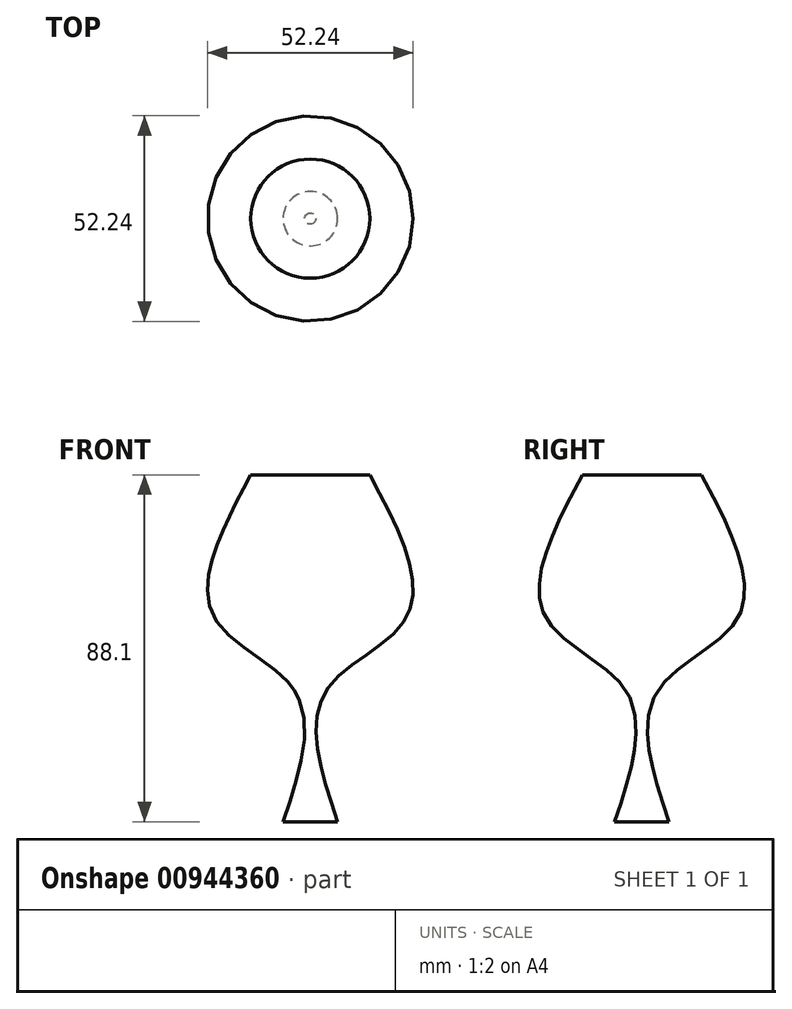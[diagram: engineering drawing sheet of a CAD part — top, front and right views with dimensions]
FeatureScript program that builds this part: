
annotation { "Feature Type Name" : "Feature", "Feature Type Description" : "" }
export const myFeature = defineFeature(function(context is Context, id is Id, definition is map)
    precondition{}
    {
        {
            var Q0;
            Q0=qCreatedBy(makeId("Top.planeOp"),FACE);
            var sketch = newSketch(context, id + "F0", { "sketchPlane" : qUnion([Q0])});
            skCircle(sketch, "E0", {"center": v(0, 0) * mm, "radius": 6.91 * mm});
            skSolve(sketch);
        }
        {
            var Q0;
            Q0=qCreatedBy(makeId("Top.planeOp"),FACE);
            cPlane(context, id + "F1", {"entities" : qUnion([Q0]), "cplaneType" : CPlaneType.OFFSET, "offset" : 88.1 * mm, "width" : 150 * mm, "height" : 150 * mm});
        }
        {
            var Q0;
            Q0=qCreatedBy(id+"F1.planeOp",FACE);
            var sketch = newSketch(context, id + "F2", { "sketchPlane" : qUnion([Q0])});
            skCircle(sketch, "E1", {"center": v(0, 0) * mm, "radius": 15.13 * mm});
            skSolve(sketch);
        }
        {
            var Q0;
            Q0=qCreatedBy(makeId("Top.planeOp"),FACE);
            cPlane(context, id + "F3", {"entities" : qUnion([Q0]), "cplaneType" : CPlaneType.OFFSET, "offset" : 34 * mm, "width" : 150 * mm, "height" : 150 * mm});
        }
        {
            var Q0;
            Q0=qCreatedBy(id+"F3.planeOp",FACE);
            var sketch = newSketch(context, id + "F4", { "sketchPlane" : qUnion([Q0])});
            skCircle(sketch, "E2", {"center": v(0, 0) * mm, "radius": 4.5 * mm});
            skSolve(sketch);
        }
        {
            var Q0;
            Q0=qCreatedBy(makeId("Top.planeOp"),FACE);
            cPlane(context, id + "F5", {"entities" : qUnion([Q0]), "cplaneType" : CPlaneType.OFFSET, "offset" : 50.6 * mm, "width" : 150 * mm, "height" : 150 * mm});
        }
        {
            var Q0;
            Q0=qCreatedBy(id+"F5.planeOp",FACE);
            var sketch = newSketch(context, id + "F6", { "sketchPlane" : qUnion([Q0])});
            skCircle(sketch, "E3", {"center": v(0, 0) * mm, "radius": 23.66 * mm});
            skSolve(sketch);
        }
        {
            var Q0;
            Q0=makeQuery(id+"F2.imprint","IMPRINT",FACE,{"disambiguationData":[TD([[makeQuery(id+"F2.imprint","IMPRINT",EDGE,{"derivedFrom":sQuery(id+"F2.wireOp",EDGE,"E1")}),1.0]])]});
            var Q1;
            Q1=makeQuery(id+"F6.imprint","IMPRINT",FACE,{"disambiguationData":[TD([[makeQuery(id+"F6.imprint","IMPRINT",EDGE,{"derivedFrom":sQuery(id+"F6.wireOp",EDGE,"E3")}),1.0]])]});
            var Q2;
            Q2=makeQuery(id+"F4.imprint","IMPRINT",FACE,{"disambiguationData":[TD([[makeQuery(id+"F4.imprint","IMPRINT",EDGE,{"derivedFrom":sQuery(id+"F4.wireOp",EDGE,"E2")}),1.0]])]});
            var Q3;
            Q3=makeQuery(id+"F0.imprint","IMPRINT",FACE,{"disambiguationData":[TD([[makeQuery(id+"F0.imprint","IMPRINT",EDGE,{"derivedFrom":sQuery(id+"F0.wireOp",EDGE,"E0")}),1.0]])]});
            loft(context, id + "F7", {"sheetProfilesArray" : [{ "sheetProfileEntities" : qUnion([Q0]) }, { "sheetProfileEntities" : qUnion([Q1]) }, { "sheetProfileEntities" : qUnion([Q2]) }, { "sheetProfileEntities" : qUnion([Q3]) }]});
        }
    });
